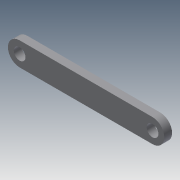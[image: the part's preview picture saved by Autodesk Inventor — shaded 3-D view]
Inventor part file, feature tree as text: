
AUTODESK INVENTOR PART (.ipt)
format: ipt  version: 2013 (Build 170138000, 138)  size: 84,480 bytes
history: native  units: mm
features: extrude x2, sketch x2
ambient origin geometry x8: Origin, YZ Plane, XZ Plane, XY Plane, X Axis, Y Axis, Z Axis, Center Point
bodies: Solid1 (feature_tree)
feature tree (4):
  extrude  "Extrusion1"  Depth=6.0mm
  extrude  "Extrusion2"  Depth=3.0mm
  sketch  "Sketch1"  dims[d0=34.0mm d1=6.0mm]
  sketch  "Sketch2"  dims[d2=2.0mm d3=0.0mm d4=3.0mm d5=3.0mm d6=2.0mm d7=0.0mm]
